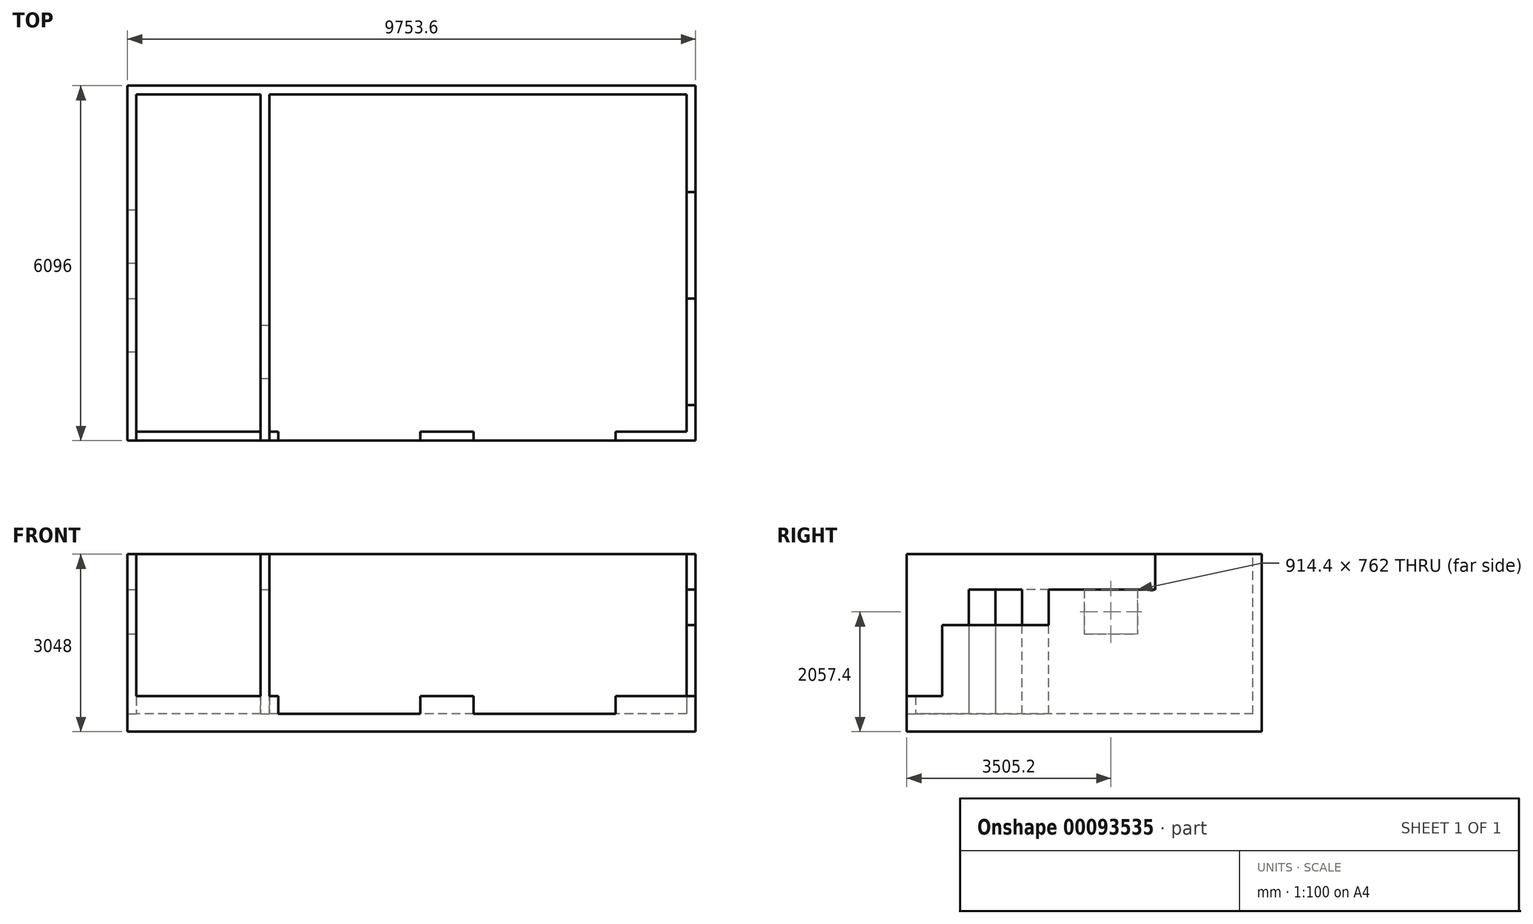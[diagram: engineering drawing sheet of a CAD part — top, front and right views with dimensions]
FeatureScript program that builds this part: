
annotation { "Feature Type Name" : "Feature", "Feature Type Description" : "" }
export const myFeature = defineFeature(function(context is Context, id is Id, definition is map)
    precondition{}
    {
        {
            var Q0;
            Q0=qCreatedBy(makeId("Top.planeOp"),FACE);
            var sketch = newSketch(context, id + "F0", { "sketchPlane" : qUnion([Q0])});
            skLineSegment(sketch, "E0.bottom", {"start": v(0, 0) * mm, "end": v(9753.6, 0) * mm});
            skLineSegment(sketch, "E0.top", {"start": v(0, 6096) * mm, "end": v(9753.6, 6096) * mm});
            skLineSegment(sketch, "E0.left", {"start": v(0, 0) * mm, "end": v(0, 6096) * mm});
            skLineSegment(sketch, "E0.right", {"start": v(9753.6, 0) * mm, "end": v(9753.6, 6096) * mm});
            skSolve(sketch);
        }
        {
            var Q0;
            Q0 = qSketchRegion(id + "F0", true);
            extrude(context, id + "F1", {"entities" : qUnion([Q0]), "depth" : 304.8 * mm});
        }
        {
            var Q0;
            Q0=makeQuery(id+"F1.opExtrude","CAP_FACE",FACE,{"disambiguationData":[OSD([sQuery(id+"F0.wireOp",EDGE,"E0.bottom"),sQuery(id+"F0.wireOp",EDGE,"E0.top"),sQuery(id+"F0.wireOp",EDGE,"E0.left"),sQuery(id+"F0.wireOp",EDGE,"E0.right")])],"isStart":false});
            var sketch = newSketch(context, id + "F2", { "sketchPlane" : qUnion([Q0])});
            skLineSegment(sketch, "E1.bottom", {"start": v(5943.6, 0) * mm, "end": v(5029.2, 0) * mm});
            skLineSegment(sketch, "E1.top", {"start": v(5943.6, 152.4) * mm, "end": v(5029.2, 152.4) * mm});
            skLineSegment(sketch, "E1.left", {"start": v(5943.6, 0) * mm, "end": v(5943.6, 152.4) * mm});
            skLineSegment(sketch, "E1.right", {"start": v(5029.2, 0) * mm, "end": v(5029.2, 152.4) * mm});
            skPoint(sketch, "E1.middle", {"position": v(5486.4, 76.2) * mm});
            skLineSegment(sketch, "E2", {"start": v(8382, 0) * mm, "end": v(9753.6, 0) * mm});
            skLineSegment(sketch, "E3", {"start": v(9753.6, 0) * mm, "end": v(9753.6, 6096) * mm});
            skLineSegment(sketch, "E4", {"start": v(9753.6, 6096) * mm, "end": v(0, 6096) * mm});
            skLineSegment(sketch, "E5", {"start": v(0, 5943.6) * mm, "end": v(9601.2, 5943.6) * mm});
            skLineSegment(sketch, "E6", {"start": v(9601.2, 5943.6) * mm, "end": v(9601.2, 152.4) * mm});
            skLineSegment(sketch, "E7", {"start": v(9601.2, 152.4) * mm, "end": v(8382, 152.4) * mm});
            skLineSegment(sketch, "E8", {"start": v(8382, 152.4) * mm, "end": v(8382, 0) * mm});
            skLineSegment(sketch, "E9", {"start": v(2590.8, 0) * mm, "end": v(2590.8, 152.4) * mm});
            skLineSegment(sketch, "E10", {"start": v(2590.8, 152.4) * mm, "end": v(152.4, 152.4) * mm});
            skLineSegment(sketch, "E11", {"start": v(152.4, 152.4) * mm, "end": v(152.4, 914.4) * mm});
            skLineSegment(sketch, "E12", {"start": v(152.4, 914.4) * mm, "end": v(0, 914.4) * mm});
            skLineSegment(sketch, "E13", {"start": v(0, 914.4) * mm, "end": v(0, 0) * mm});
            skLineSegment(sketch, "E14", {"start": v(0, 0) * mm, "end": v(2590.8, 0) * mm});
            skLineSegment(sketch, "E15", {"start": v(0, 6096) * mm, "end": v(0, 5943.6) * mm});
            skSolve(sketch);
        }
        {
            var Q0;
            Q0 = qSketchRegion(id + "F2", true);
            extrude(context, id + "F3", {"entities" : qUnion([Q0]), "operationType" : NewBodyOperationType.ADD, "depth" : 304.8 * mm});
        }
        {
            var Q0;
            Q0=makeQuery(id+"F3.opExtrude","CAP_FACE",FACE,{"disambiguationData":[OSD([sQuery(id+"F2.wireOp",EDGE,"E2"),sQuery(id+"F2.wireOp",EDGE,"E3"),sQuery(id+"F2.wireOp",EDGE,"E4"),sQuery(id+"F2.wireOp",EDGE,"CElO2aeV-4ry8-U5nN-VFw7-lKZjGSDdjc46"),sQuery(id+"F2.wireOp",EDGE,"aXI8KXb9-mfIK-bI9D-YpWg-9FVOQ1UAsdFk"),sQuery(id+"F2.wireOp",EDGE,"YwxrfCe7-5sPB-iO6G-MdUH-hFZLTdnCo4qc"),sQuery(id+"F2.wireOp",EDGE,"E5"),sQuery(id+"F2.wireOp",EDGE,"E6"),sQuery(id+"F2.wireOp",EDGE,"E7"),sQuery(id+"F2.wireOp",EDGE,"E8")])],"isStart":false});
            var sketch = newSketch(context, id + "F4", { "sketchPlane" : qUnion([Q0])});
            skLineSegment(sketch, "E16.3", {"start": v(0, 5943.6) * mm, "end": v(9601.2, 5943.6) * mm});
            skLineSegment(sketch, "E16.4", {"start": v(0, 6096) * mm, "end": v(9753.6, 6096) * mm});
            skLineSegment(sketch, "E17", {"start": v(9601.2, 5943.6) * mm, "end": v(9601.2, 4267.2) * mm});
            skLineSegment(sketch, "E18", {"start": v(9601.2, 4267.2) * mm, "end": v(9753.6, 4267.2) * mm});
            skLineSegment(sketch, "E19", {"start": v(9753.6, 4267.2) * mm, "end": v(9753.6, 6096) * mm});
            skLineSegment(sketch, "E20", {"start": v(0, 6096) * mm, "end": v(0, 5943.6) * mm});
            skSolve(sketch);
        }
        {
            var Q0;
            Q0 = qSketchRegion(id + "F4", true);
            extrude(context, id + "F5", {"entities" : qUnion([Q0]), "operationType" : NewBodyOperationType.ADD, "depth" : 2438.4 * mm});
        }
        {
            var Q0;
            Q0=makeQuery(id+"F3.opExtrude","CAP_FACE",FACE,{"disambiguationData":[OSD([sQuery(id+"F2.wireOp",EDGE,"E2"),sQuery(id+"F2.wireOp",EDGE,"E3"),sQuery(id+"F2.wireOp",EDGE,"E4"),sQuery(id+"F2.wireOp",EDGE,"CElO2aeV-4ry8-U5nN-VFw7-lKZjGSDdjc46"),sQuery(id+"F2.wireOp",EDGE,"aXI8KXb9-mfIK-bI9D-YpWg-9FVOQ1UAsdFk"),sQuery(id+"F2.wireOp",EDGE,"YwxrfCe7-5sPB-iO6G-MdUH-hFZLTdnCo4qc"),sQuery(id+"F2.wireOp",EDGE,"E5"),sQuery(id+"F2.wireOp",EDGE,"E6"),sQuery(id+"F2.wireOp",EDGE,"E7"),sQuery(id+"F2.wireOp",EDGE,"E8")])],"isStart":false});
            var sketch = newSketch(context, id + "F6", { "sketchPlane" : qUnion([Q0])});
            skLineSegment(sketch, "E21.bottom", {"start": v(9601.2, 4267.2) * mm, "end": v(9753.6, 4267.2) * mm});
            skLineSegment(sketch, "E21.top", {"start": v(9601.2, 2438.4) * mm, "end": v(9753.6, 2438.4) * mm});
            skLineSegment(sketch, "E21.left", {"start": v(9601.2, 4267.2) * mm, "end": v(9601.2, 2438.4) * mm});
            skLineSegment(sketch, "E21.right", {"start": v(9753.6, 4267.2) * mm, "end": v(9753.6, 2438.4) * mm});
            skSolve(sketch);
        }
        {
            var Q0;
            Q0 = qSketchRegion(id + "F6", true);
            extrude(context, id + "F7", {"entities" : qUnion([Q0]), "operationType" : NewBodyOperationType.ADD, "depth" : 1828.8 * mm});
        }
        {
            var Q0;
            Q0=makeQuery(id+"F3.opExtrude","CAP_FACE",FACE,{"disambiguationData":[OSD([sQuery(id+"F2.wireOp",EDGE,"E2"),sQuery(id+"F2.wireOp",EDGE,"E3"),sQuery(id+"F2.wireOp",EDGE,"E4"),sQuery(id+"F2.wireOp",EDGE,"CElO2aeV-4ry8-U5nN-VFw7-lKZjGSDdjc46"),sQuery(id+"F2.wireOp",EDGE,"aXI8KXb9-mfIK-bI9D-YpWg-9FVOQ1UAsdFk"),sQuery(id+"F2.wireOp",EDGE,"YwxrfCe7-5sPB-iO6G-MdUH-hFZLTdnCo4qc"),sQuery(id+"F2.wireOp",EDGE,"E5"),sQuery(id+"F2.wireOp",EDGE,"E6"),sQuery(id+"F2.wireOp",EDGE,"E7"),sQuery(id+"F2.wireOp",EDGE,"E8")])],"isStart":false});
            var sketch = newSketch(context, id + "F8", { "sketchPlane" : qUnion([Q0])});
            skLineSegment(sketch, "E22.bottom", {"start": v(9601.2, 2438.4) * mm, "end": v(9753.6, 2438.4) * mm});
            skLineSegment(sketch, "E22.top", {"start": v(9601.2, 609.6) * mm, "end": v(9753.6, 609.6) * mm});
            skLineSegment(sketch, "E22.left", {"start": v(9601.2, 2438.4) * mm, "end": v(9601.2, 609.6) * mm});
            skLineSegment(sketch, "E22.right", {"start": v(9753.6, 2438.4) * mm, "end": v(9753.6, 609.6) * mm});
            skSolve(sketch);
        }
        {
            var Q0;
            Q0 = qSketchRegion(id + "F8", true);
            extrude(context, id + "F9", {"entities" : qUnion([Q0]), "operationType" : NewBodyOperationType.ADD, "depth" : 1219.2 * mm});
        }
        {
            var Q0;
            Q0=makeQuery(id+"F3.opExtrude","SWEPT_FACE",FACE,{"disambiguationData":[OSD([sQuery(id+"F2.wireOp",EDGE,"E9")])]});
            var sketch = newSketch(context, id + "F10", { "sketchPlane" : qUnion([Q0])});
            skLineSegment(sketch, "E23", {"start": v(0, 609.6) * mm, "end": v(0, 3048) * mm});
            skLineSegment(sketch, "E24.0", {"start": v(5943.6, 304.8) * mm, "end": v(5943.6, 3048) * mm});
            skLineSegment(sketch, "E25", {"start": v(5943.6, 3048) * mm, "end": v(0, 3048) * mm});
            skLineSegment(sketch, "E26", {"start": v(5943.6, 304.8) * mm, "end": v(1981.2, 304.8) * mm});
            skLineSegment(sketch, "E27", {"start": v(1981.2, 304.8) * mm, "end": v(1981.2, 2438.4) * mm});
            skLineSegment(sketch, "E28", {"start": v(1981.2, 2438.4) * mm, "end": v(1066.8, 2438.4) * mm});
            skLineSegment(sketch, "E29", {"start": v(1066.8, 2438.4) * mm, "end": v(1066.8, 304.8) * mm});
            skLineSegment(sketch, "E30", {"start": v(1066.8, 304.8) * mm, "end": v(152.4, 304.8) * mm});
            skLineSegment(sketch, "E31", {"start": v(152.4, 304.8) * mm, "end": v(152.4, 609.6) * mm});
            skLineSegment(sketch, "E32", {"start": v(152.4, 609.6) * mm, "end": v(0, 609.6) * mm});
            skSolve(sketch);
        }
        {
            var Q0;
            Q0 = qSketchRegion(id + "F10", true);
            extrude(context, id + "F11", {"entities" : qUnion([Q0]), "operationType" : NewBodyOperationType.ADD, "oppositeDirection" : true, "depth" : 304.8 * mm, "hasSecondDirection" : true, "secondDirectionOppositeDirection" : true, "secondDirectionDepth" : 152.4 * mm});
        }
        {
            var Q0;
            Q0=makeQuery(id+"F3.opExtrude","SWEPT_FACE",FACE,{"disambiguationData":[OSD([sQuery(id+"F2.wireOp",EDGE,"E9")])]});
            var sketch = newSketch(context, id + "F12", { "sketchPlane" : qUnion([Q0])});
            skLineSegment(sketch, "E33.0", {"start": v(0, 304.8) * mm, "end": v(152.4, 304.8) * mm});
            skLineSegment(sketch, "E33.1", {"start": v(0, 609.6) * mm, "end": v(0, 304.8) * mm});
            skLineSegment(sketch, "E34.0", {"start": v(5943.6, 3048) * mm, "end": v(5943.6, 304.8) * mm});
            skLineSegment(sketch, "E35.0", {"start": v(5943.6, 3048) * mm, "end": v(0, 3048) * mm});
            skLineSegment(sketch, "E36.0", {"start": v(0, 609.6) * mm, "end": v(0, 3048) * mm});
            skLineSegment(sketch, "E37", {"start": v(5943.6, 304.8) * mm, "end": v(2438.4, 304.8) * mm});
            skLineSegment(sketch, "E38", {"start": v(2438.4, 304.8) * mm, "end": v(2438.4, 2438.4) * mm});
            skLineSegment(sketch, "E39", {"start": v(2438.4, 2438.4) * mm, "end": v(1524, 2438.4) * mm});
            skLineSegment(sketch, "E40", {"start": v(1524, 2438.4) * mm, "end": v(1524, 304.8) * mm});
            skLineSegment(sketch, "E41", {"start": v(1524, 304.8) * mm, "end": v(152.4, 304.8) * mm});
            skLineSegment(sketch, "E42.bottom", {"start": v(3048, 2438.4) * mm, "end": v(3962.4, 2438.4) * mm});
            skLineSegment(sketch, "E42.top", {"start": v(3048, 1676.4) * mm, "end": v(3962.4, 1676.4) * mm});
            skLineSegment(sketch, "E42.left", {"start": v(3048, 2438.4) * mm, "end": v(3048, 1676.4) * mm});
            skLineSegment(sketch, "E42.right", {"start": v(3962.4, 2438.4) * mm, "end": v(3962.4, 1676.4) * mm});
            skSolve(sketch);
        }
        {
            var Q0;
            Q0 = qSketchRegion(id + "F12", true);
            extrude(context, id + "F13", {"entities" : qUnion([Q0]), "operationType" : NewBodyOperationType.ADD, "oppositeDirection" : true, "depth" : 2590.8 * mm, "hasSecondDirection" : true, "secondDirectionOppositeDirection" : true, "secondDirectionDepth" : 2438.4 * mm});
        }
    });
